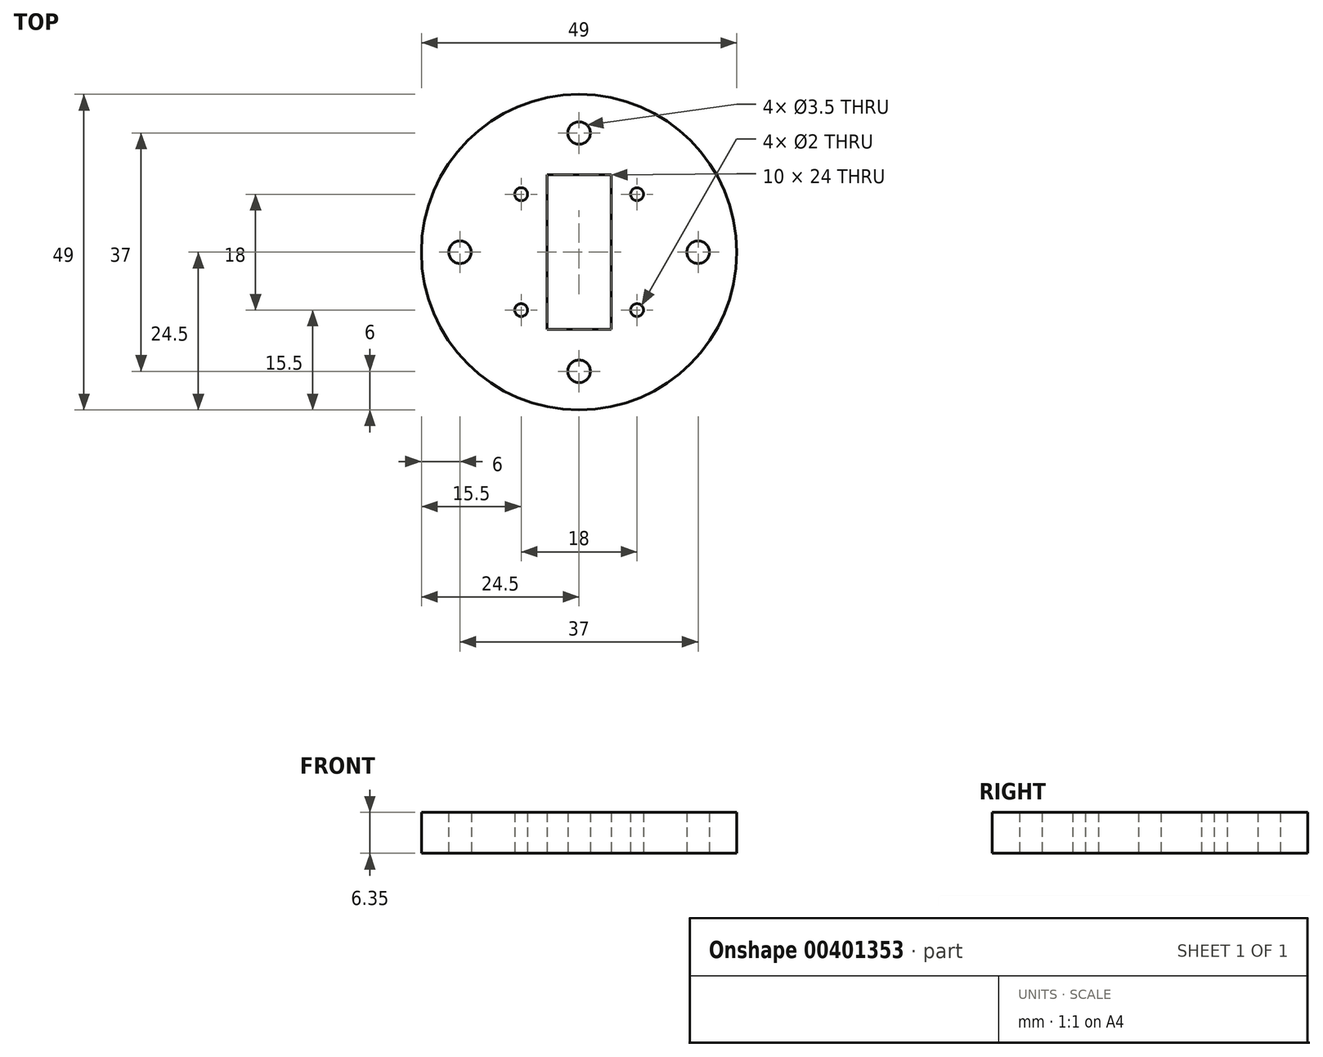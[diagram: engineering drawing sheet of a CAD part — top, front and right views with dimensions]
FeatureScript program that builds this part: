
annotation { "Feature Type Name" : "Feature", "Feature Type Description" : "" }
export const myFeature = defineFeature(function(context is Context, id is Id, definition is map)
    precondition{}
    {
        {
            var Q0;
            Q0=qCreatedBy(makeId("Top.planeOp"),FACE);
            var sketch = newSketch(context, id + "F0", { "sketchPlane" : qUnion([Q0])});
            skCircle(sketch, "E0", {"center": v(0, 0) * mm, "radius": 24.5 * mm});
            skLineSegment(sketch, "E1", {"start": v(-24.5, 0) * mm, "end": v(24.5, 0) * mm, "construction": true});
            skLineSegment(sketch, "E2", {"start": v(0, 0) * mm, "end": v(0, 24.5) * mm, "construction": true});
            skLineSegment(sketch, "E3", {"start": v(0, 24.5) * mm, "end": v(0, -24.5) * mm, "construction": true});
            skCircle(sketch, "E4", {"center": v(-18.5, 0) * mm, "radius": 1.75 * mm});
            skCircle(sketch, "E5", {"center": v(0, 18.5) * mm, "radius": 1.75 * mm});
            skCircle(sketch, "E6", {"center": v(18.5, 0) * mm, "radius": 1.75 * mm});
            skCircle(sketch, "E7", {"center": v(0, -18.5) * mm, "radius": 1.75 * mm});
            skLineSegment(sketch, "E8.bottom", {"start": v(-5, 12) * mm, "end": v(5, 12) * mm});
            skLineSegment(sketch, "E8.top", {"start": v(-5, -12) * mm, "end": v(5, -12) * mm});
            skLineSegment(sketch, "E8.left", {"start": v(-5, 12) * mm, "end": v(-5, -12) * mm});
            skLineSegment(sketch, "E8.right", {"start": v(5, 12) * mm, "end": v(5, -12) * mm});
            skLineSegment(sketch, "E9", {"start": v(-11.2, 9) * mm, "end": v(12.23, 9) * mm, "construction": true});
            skLineSegment(sketch, "E10", {"start": v(-11.62, -9) * mm, "end": v(11.3, -9) * mm, "construction": true});
            skLineSegment(sketch, "E11", {"start": v(9, 14.61) * mm, "end": v(9, -12.56) * mm, "construction": true});
            skLineSegment(sketch, "E12", {"start": v(-9, 14.19) * mm, "end": v(-9, -14.35) * mm, "construction": true});
            skCircle(sketch, "E13", {"center": v(9, 9) * mm, "radius": 1 * mm});
            skCircle(sketch, "E14", {"center": v(9, -9) * mm, "radius": 1 * mm});
            skCircle(sketch, "E15", {"center": v(-9, -9) * mm, "radius": 1 * mm});
            skCircle(sketch, "E16", {"center": v(-9, 9) * mm, "radius": 1 * mm});
            skSolve(sketch);
        }
        {
            var Q0;
            Q0=makeQuery(id+"F0.imprint","IMPRINT",FACE,{"disambiguationData":[TD([[makeQuery(id+"F0.imprint","IMPRINT",EDGE,{"derivedFrom":sQuery(id+"F0.wireOp",EDGE,"E0")}),1.0]])]});
            extrude(context, id + "F1", {"entities" : qUnion([Q0]), "depth" : 6.35 * mm, "offsetDistance" : 25 * mm});
        }
    });
